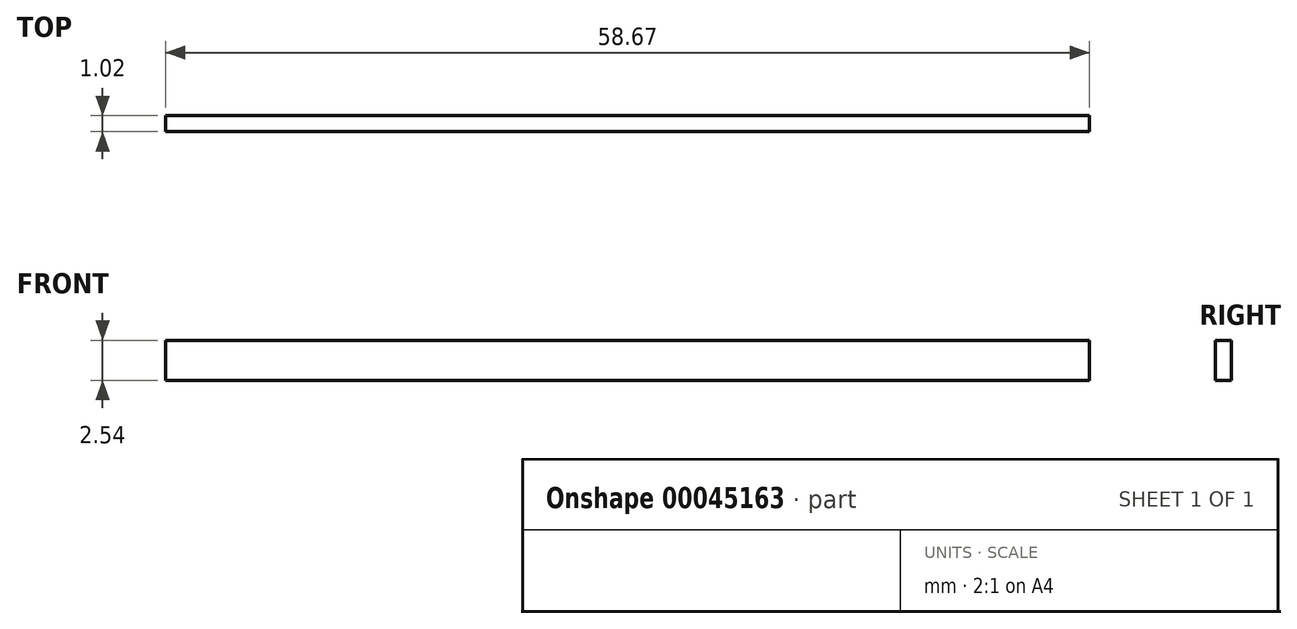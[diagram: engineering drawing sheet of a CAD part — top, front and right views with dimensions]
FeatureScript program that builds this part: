
annotation { "Feature Type Name" : "Feature", "Feature Type Description" : "" }
export const myFeature = defineFeature(function(context is Context, id is Id, definition is map)
    precondition{}
    {
        {
            var Q0;
            Q0=qCreatedBy(makeId("Front.planeOp"),FACE);
            var sketch = newSketch(context, id + "F0", { "sketchPlane" : qUnion([Q0])});
            skLineSegment(sketch, "E0", {"start": v(0, 0) * mm, "end": v(58.67, 0) * mm});
            skLineSegment(sketch, "E1", {"start": v(58.67, 0) * mm, "end": v(58.67, 2.54) * mm});
            skLineSegment(sketch, "E2", {"start": v(58.67, 2.54) * mm, "end": v(0, 2.54) * mm});
            skLineSegment(sketch, "E3", {"start": v(0, 2.54) * mm, "end": v(0, 0) * mm});
            skSolve(sketch);
        }
        {
            var Q0;
            Q0 = qSketchRegion(id + "F0", true);
            extrude(context, id + "F1", {"entities" : qUnion([Q0]), "depth" : 1.02 * mm});
        }
    });
